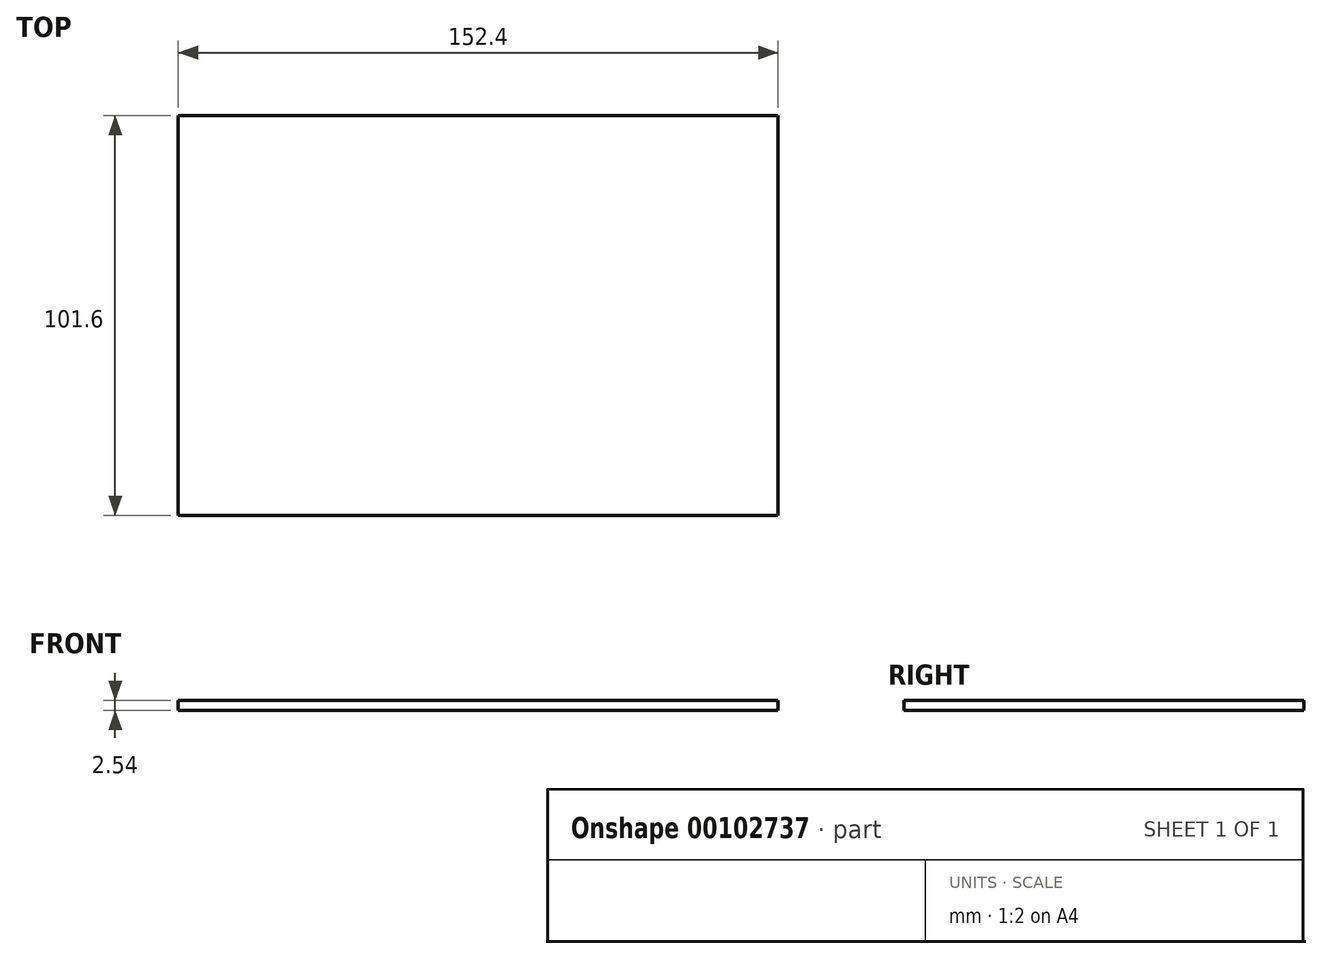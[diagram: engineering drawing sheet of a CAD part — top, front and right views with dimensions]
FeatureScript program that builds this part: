
annotation { "Feature Type Name" : "Feature", "Feature Type Description" : "" }
export const myFeature = defineFeature(function(context is Context, id is Id, definition is map)
    precondition{}
    {
        {
            var Q0;
            Q0=qCreatedBy(makeId("Top.planeOp"),FACE);
            var sketch = newSketch(context, id + "F0", { "sketchPlane" : qUnion([Q0])});
            skLineSegment(sketch, "E0.bottom", {"start": v(-1058.96, 188.8) * mm, "end": v(-906.56, 188.8) * mm});
            skLineSegment(sketch, "E0.top", {"start": v(-1058.96, 87.2) * mm, "end": v(-906.56, 87.2) * mm});
            skLineSegment(sketch, "E0.left", {"start": v(-1058.96, 188.8) * mm, "end": v(-1058.96, 87.2) * mm});
            skLineSegment(sketch, "E0.right", {"start": v(-906.56, 188.8) * mm, "end": v(-906.56, 87.2) * mm});
            skSolve(sketch);
        }
        {
            var Q0;
            Q0 = qSketchRegion(id + "F0", true);
            extrude(context, id + "F1", {"entities" : qUnion([Q0]), "depth" : 2.54 * mm});
        }
    });
